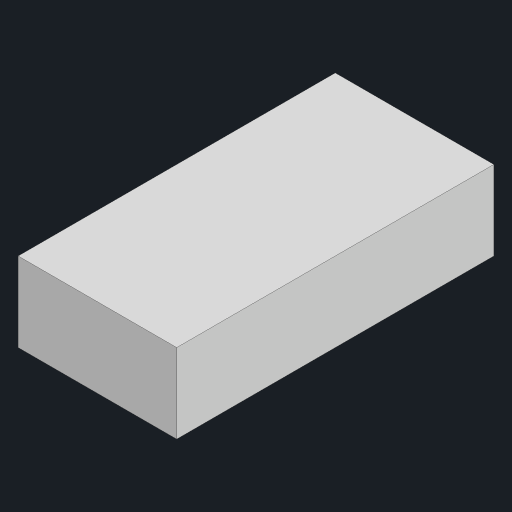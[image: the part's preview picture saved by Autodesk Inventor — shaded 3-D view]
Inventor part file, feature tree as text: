
AUTODESK INVENTOR PART (.ipt)
format: ipt  version: 2023.1 (Build 271208000, 208)  size: 80,384 bytes
history: native  units: mm
features: extrude x1, sketch x1
ambient origin geometry x8: Origin, YZ Plane, XZ Plane, XY Plane, X Axis, Y Axis, Z Axis, Center Point
bodies: Solid1 (feature_tree)
feature tree (2):
  extrude  "Extrusion1"  Depth=203.2mm
  sketch  "Sketch1"  dims[d0=101.6mm d1=203.2mm d2=50.8mm d3=0.0mm]
